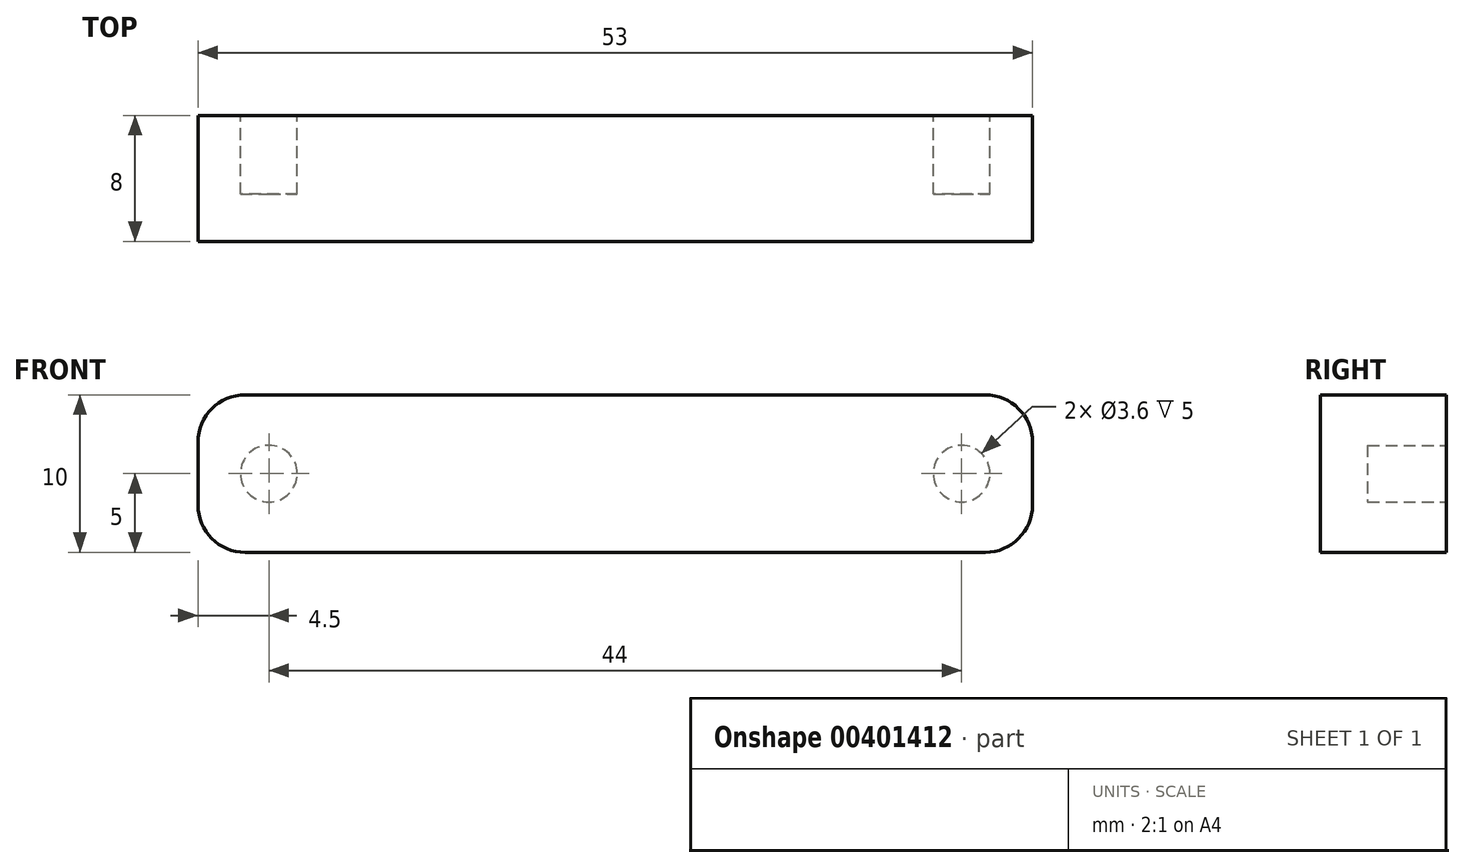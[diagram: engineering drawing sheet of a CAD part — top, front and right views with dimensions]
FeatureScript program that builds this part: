
annotation { "Feature Type Name" : "Feature", "Feature Type Description" : "" }
export const myFeature = defineFeature(function(context is Context, id is Id, definition is map)
    precondition{}
    {
        {
            var Q0;
            Q0=qCreatedBy(makeId("Front.planeOp"),FACE);
            var sketch = newSketch(context, id + "F0", { "sketchPlane" : qUnion([Q0])});
            skLineSegment(sketch, "E0.bottom", {"start": v(0, 0) * mm, "end": v(-53, 0) * mm});
            skLineSegment(sketch, "E0.top", {"start": v(0, 10) * mm, "end": v(-53, 10) * mm});
            skLineSegment(sketch, "E0.left", {"start": v(0, 0) * mm, "end": v(0, 10) * mm});
            skLineSegment(sketch, "E0.right", {"start": v(-53, 0) * mm, "end": v(-53, 10) * mm});
            skCircle(sketch, "E1", {"center": v(-48.5, 5) * mm, "radius": 1.8 * mm});
            skPoint(sketch, "E1.centerSnap0", {"position": v(-53, 5) * mm});
            skCircle(sketch, "E2", {"center": v(-4.5, 5) * mm, "radius": 1.8 * mm});
            skPoint(sketch, "E2.centerSnap0", {"position": v(0, 5) * mm});
            skSolve(sketch);
        }
        {
            var Q0;
            Q0 = qSketchRegion(id + "F0", true);
            var Q1;
            Q1=makeQuery(id+"F0.imprint","IMPRINT",FACE,{"disambiguationData":[TD([[makeQuery(id+"F0.imprint","IMPRINT",EDGE,{"derivedFrom":sQuery(id+"F0.wireOp",EDGE,"E1")}),1.0]])]});
            var Q2;
            Q2=makeQuery(id+"F0.imprint","IMPRINT",FACE,{"disambiguationData":[TD([[makeQuery(id+"F0.imprint","IMPRINT",EDGE,{"derivedFrom":sQuery(id+"F0.wireOp",EDGE,"E2")}),1.0]])]});
            extrude(context, id + "F1", {"entities" : qUnion([Q0, Q1, Q2]), "depth" : 8 * mm});
        }
        {
            var Q0;
            Q0=makeQuery(id+"F1.opExtrude","CAP_FACE",FACE,{"disambiguationData":[OSD([sQuery(id+"F0.wireOp",EDGE,"E0.bottom"),sQuery(id+"F0.wireOp",EDGE,"E0.top"),sQuery(id+"F0.wireOp",EDGE,"E0.left"),sQuery(id+"F0.wireOp",EDGE,"E0.right")])],"isStart":true});
            var sketch = newSketch(context, id + "F2", { "sketchPlane" : qUnion([Q0])});
            skCircle(sketch, "E3", {"center": v(4.5, 5) * mm, "radius": 1.8 * mm});
            skPoint(sketch, "E3.centerSnap0", {"position": v(0, 5) * mm});
            skCircle(sketch, "E4", {"center": v(48.5, 5) * mm, "radius": 1.8 * mm});
            skSolve(sketch);
        }
        {
            var Q0;
            Q0 = qSketchRegion(id + "F2", true);
            extrude(context, id + "F3", {"entities" : qUnion([Q0]), "operationType" : NewBodyOperationType.REMOVE, "oppositeDirection" : true, "depth" : 5 * mm});
        }
        {
            var Q0;
            Q0=makeQuery(id+"F1.opExtrude","SWEPT_EDGE",EDGE,{"disambiguationData":[OSD([sQuery(id+"F0.wireOp",EDGE,"E0.top"),sQuery(id+"F0.wireOp",EDGE,"E0.left")])]});
            var Q1;
            Q1=makeQuery(id+"F1.opExtrude","SWEPT_EDGE",EDGE,{"disambiguationData":[OSD([sQuery(id+"F0.wireOp",EDGE,"E0.bottom"),sQuery(id+"F0.wireOp",EDGE,"E0.left")])]});
            var Q2;
            Q2=makeQuery(id+"F1.opExtrude","SWEPT_EDGE",EDGE,{"disambiguationData":[OSD([sQuery(id+"F0.wireOp",EDGE,"E0.top"),sQuery(id+"F0.wireOp",EDGE,"E0.right")])]});
            var Q3;
            Q3=makeQuery(id+"F1.opExtrude","SWEPT_EDGE",EDGE,{"disambiguationData":[OSD([sQuery(id+"F0.wireOp",EDGE,"E0.bottom"),sQuery(id+"F0.wireOp",EDGE,"E0.right")])]});
            fillet(context, id + "F4", {"entities" : qUnion([Q0, Q1, Q2, Q3]), "radius" : 3 * mm, "tangentPropagation" : true, "allowEdgeOverflow" : false});
        }
    });
